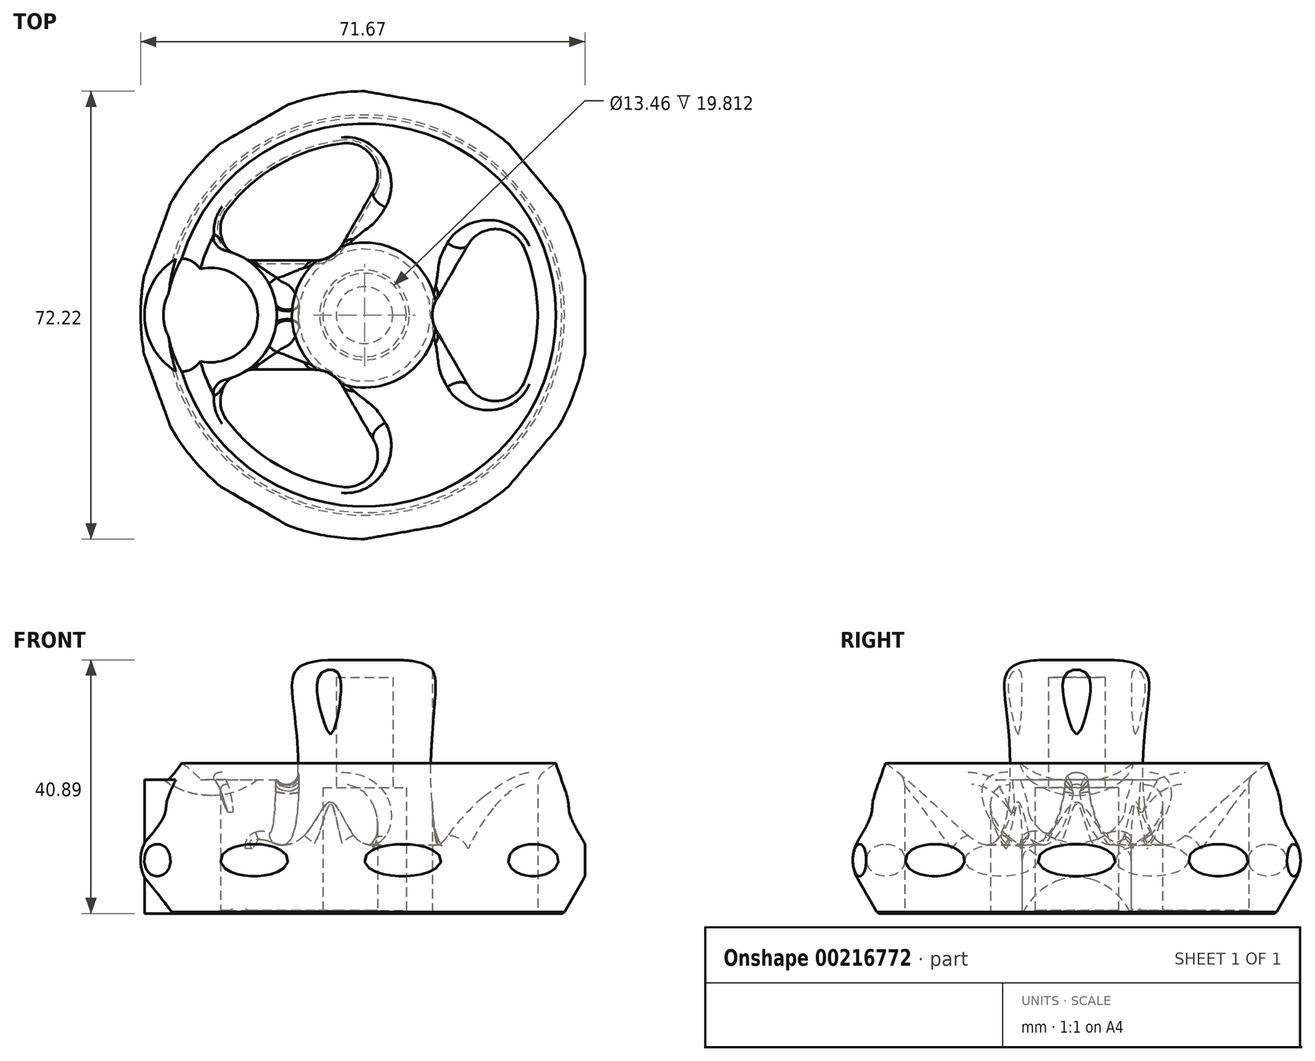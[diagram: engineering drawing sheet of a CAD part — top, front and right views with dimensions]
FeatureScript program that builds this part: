
annotation { "Feature Type Name" : "Feature", "Feature Type Description" : "" }
export const myFeature = defineFeature(function(context is Context, id is Id, definition is map)
    precondition{}
    {
        {
            var Q0;
            Q0=qCreatedBy(makeId("Front.planeOp"),FACE);
            var sketch = newSketch(context, id + "F0", { "sketchPlane" : qUnion([Q0])});
            skLineSegment(sketch, "E0", {"start": v(6.73, 0) * mm, "end": v(32.13, 0) * mm});
            skLineSegment(sketch, "E1", {"start": v(0, 40.64) * mm, "end": v(0, 38.1) * mm});
            skLineSegment(sketch, "E2", {"start": v(0, 38.1) * mm, "end": v(4.57, 38.1) * mm});
            skLineSegment(sketch, "E3", {"start": v(6.73, 20.32) * mm, "end": v(6.73, 0) * mm});
            skFitSpline(sketch, "E4", {"points": [v(35.65, 24.88) * mm, v(14.9, 11.07) * mm, v(10.97, 29.16) * mm, v(10.85, 39.41) * mm, v(0, 40.64) * mm], "startDerivative": vector(-45.35, 35.18) * mm, "endDerivative": vector(-73, -6.21) * mm});
            skPoint(sketch, "E5.orphan", {"position": v(0, 77.97) * mm});
            skLineSegment(sketch, "E6", {"start": v(0, -42.76) * mm, "end": v(0, 58.59) * mm, "construction": true});
            skLineSegment(sketch, "E7", {"start": v(4.57, 38.1) * mm, "end": v(4.57, 20.32) * mm});
            skLineSegment(sketch, "E8", {"start": v(4.57, 20.32) * mm, "end": v(6.73, 20.32) * mm});
            skPoint(sketch, "E9.orphan", {"position": v(11.05, 17.05) * mm});
            skLineSegment(sketch, "E10", {"start": v(32.13, 0) * mm, "end": v(35.26, 5.42) * mm});
            skPoint(sketch, "E11.visualSharp", {"position": v(28.42, 22.4) * mm});
            skPoint(sketch, "E12.visualSharp", {"position": v(35.56, 5.94) * mm});
            skLineSegment(sketch, "E13", {"start": v(37.21, 8.8) * mm, "end": v(30.06, 35.48) * mm, "construction": true});
            skFitSpline(sketch, "E14", {"points": [v(37.21, 8.8) * mm, v(32.84, 18.2) * mm, v(30.88, 24.23) * mm], "startDerivative": vector(-26.8, 39.37) * mm, "endDerivative": vector(-3.75, 13.08) * mm});
            skArc(sketch, "E15.filletArc", {"start": v(33.08, 16.25) * mm, "mid": v(29.56, 20.04) * mm, "end": v(24.55, 18.79) * mm});
            skArc(sketch, "E16.filletArc", {"start": v(35.26, 5.42) * mm, "mid": v(36.11, 8.69) * mm, "end": v(35.16, 11.93) * mm});
            skSolve(sketch);
        }
        {
            var Q0;
            Q0=qSketchRegion(id+"F0",true);
            var Q1;
            Q1=sQuery(id+"F0.wireOp",EDGE,"E6");
            revolve(context, id + "F1", {"entities" : qUnion([Q0]), "axis" : qUnion([Q1]), "revolveType" : RevolveType.SYMMETRIC, "angle" : 120 * degree});
        }
        {
            var Q0;
            Q0=qCreatedBy(makeId("Top.planeOp"),FACE);
            var sketch = newSketch(context, id + "F2", { "sketchPlane" : qUnion([Q0])});
            skArc(sketch, "E17", {"start": v(25.8, -10.75) * mm, "mid": v(27.94, 0) * mm, "end": v(25.8, 10.75) * mm});
            skLineSegment(sketch, "E18", {"start": v(11.63, 2.54) * mm, "end": v(16.7, 11.33) * mm});
            skLineSegment(sketch, "E19", {"start": v(11.63, -2.54) * mm, "end": v(16.7, -11.33) * mm});
            skPoint(sketch, "E20.visualSharp", {"position": v(20.88, 18.57) * mm});
            skArc(sketch, "E20.filletArc", {"start": v(25.8, 10.75) * mm, "mid": v(21.43, 13.86) * mm, "end": v(16.7, 11.33) * mm});
            skPoint(sketch, "E21.visualSharp", {"position": v(20.88, -18.57) * mm});
            skArc(sketch, "E21.filletArc", {"start": v(16.7, -11.33) * mm, "mid": v(21.43, -13.86) * mm, "end": v(25.8, -10.75) * mm});
            skPoint(sketch, "E22.visualSharp", {"position": v(10.16, 0) * mm});
            skArc(sketch, "E22.filletArc", {"start": v(11.63, 2.54) * mm, "mid": v(10.95, 0) * mm, "end": v(11.63, -2.54) * mm});
            skSolve(sketch);
        }
        {
            var Q0;
            Q0=qSketchRegion(id+"F2",true);
            extrude(context, id + "F3", {"entities" : qUnion([Q0]), "operationType" : NewBodyOperationType.REMOVE, "endBound" : BoundingType.THROUGH_ALL, "depth" : 25.4 * mm});
        }
        {
            var Q0;
            Q0=makeQuery(id+"F3.boolean.opBoolean","INTERSECT",EDGE,{"derivedFrom":[makeQuery(id+"F1.opRevolve","SWEPT_FACE",FACE,{"disambiguationData":[OSD([sQuery(id+"F0.wireOp",EDGE,"E4")])]}),makeQuery(id+"F3.opExtrude","SWEPT_FACE",FACE,{"disambiguationData":[OSD([sQuery(id+"F2.wireOp",EDGE,"E17")])]})]});
            fillet(context, id + "F4", {"entities" : qUnion([Q0]), "radius" : 2.54 * mm, "tangentPropagation" : true, "allowEdgeOverflow" : false});
        }
        {
            var Q0;
            Q0=qCreatedBy(makeId("Top.planeOp"),FACE);
            var sketch = newSketch(context, id + "F5", { "sketchPlane" : qUnion([Q0])});
            skLineSegment(sketch, "E23", {"start": v(35.56, -10.16) * mm, "end": v(35.56, 10.16) * mm});
            skLineSegment(sketch, "E24", {"start": v(35.56, 10.16) * mm, "end": v(39.7, 10.16) * mm});
            skLineSegment(sketch, "E25", {"start": v(39.7, 10.16) * mm, "end": v(39.7, -10.16) * mm});
            skLineSegment(sketch, "E26", {"start": v(39.7, -10.16) * mm, "end": v(35.56, -10.16) * mm});
            skSolve(sketch);
        }
        {
            var Q0;
            Q0=qSketchRegion(id+"F5",true);
            extrude(context, id + "F6", {"entities" : qUnion([Q0]), "depth" : 25.4 * mm});
        }
        {
            var Q0;
            Q0=makeQuery(id+"F6.opExtrude","SWEPT_BODY",BODY,{"disambiguationData":[OSD([sQuery(id+"F5.wireOp",EDGE,"E23"),sQuery(id+"F5.wireOp",EDGE,"E24"),sQuery(id+"F5.wireOp",EDGE,"E25"),sQuery(id+"F5.wireOp",EDGE,"E26")])]});
            var Q1;
            Q1=sQuery(id+"F0.wireOp",EDGE,"E6");
            circularPattern(context, id + "F7", {"operationType" : NewBodyOperationType.REMOVE, "entities" : qUnion([Q0]), "axis" : qUnion([Q1]), "angle" : 360 * degree, "instanceCount" : 9, "equalSpace" : true});
        }
        {
            var Q0;
            Q0=makeQuery(id+"F1.opRevolve","SWEPT_BODY",BODY,{"disambiguationData":[OSD([sQuery(id+"F0.wireOp",EDGE,"E0"),sQuery(id+"F0.wireOp",EDGE,"dpCK8SRb-WdQn-L2Cs-7aav-e22ffPn0EV3C"),sQuery(id+"F0.wireOp",EDGE,"99iCUp3l-W3Re-Ts3m-6MKF-OaPGGpgDnCRw"),sQuery(id+"F0.wireOp",EDGE,"E1"),sQuery(id+"F0.wireOp",EDGE,"E2"),sQuery(id+"F0.wireOp",EDGE,"E3"),sQuery(id+"F0.wireOp",EDGE,"E4")])]});
            var Q1;
            Q1=sQuery(id+"F0.wireOp",EDGE,"E6");
            circularPattern(context, id + "F8", {"operationType" : NewBodyOperationType.ADD, "entities" : qUnion([Q0]), "axis" : qUnion([Q1]), "angle" : 360 * degree, "instanceCount" : 3, "equalSpace" : true});
        }
        {
            var Q0;
            Q0=makeQuery(id+"F8.opPattern","COPY",FACE,{"derivedFrom":makeQuery(id+"F3.boolean.opBoolean","COPY",FACE,{"derivedFrom":makeQuery(id+"F3.opExtrude","SWEPT_FACE",FACE,{"disambiguationData":[OSD([sQuery(id+"F2.wireOp",EDGE,"E18")])]})}),"instanceName":"1"});
            var Q1;
            {var subQ0=makeQuery(id+"F1.opRevolve","SWEPT_EDGE",EDGE,{"disambiguationData":[OSD([sQuery(id+"F0.wireOp",EDGE,"E0"),sQuery(id+"F0.wireOp",EDGE,"E3")])]});Q1=makeQuery(id+"F8.boolean.opBoolean","MERGE",EDGE,{"derivedFrom":[subQ0,makeQuery(id+"F8.opPattern","COPY",EDGE,{"derivedFrom":subQ0,"instanceName":"1"}),makeQuery(id+"F8.opPattern","COPY",EDGE,{"derivedFrom":subQ0,"instanceName":"2"})]});}
            var Q2;
            Q2=makeQuery(id+"F3.boolean.opBoolean","COPY",EDGE,{"derivedFrom":makeQuery(id+"F3.opExtrude","CAP_EDGE",EDGE,{"disambiguationData":[OSD([sQuery(id+"F2.wireOp",EDGE,"E18")])],"isStart":true})});
            var Q3;
            Q3=makeQuery(id+"F8.opPattern","COPY",EDGE,{"derivedFrom":makeQuery(id+"F3.boolean.opBoolean","COPY",EDGE,{"derivedFrom":makeQuery(id+"F3.opExtrude","CAP_EDGE",EDGE,{"disambiguationData":[OSD([sQuery(id+"F2.wireOp",EDGE,"E19")])],"isStart":true})}),"instanceName":"2"});
            var Q4;
            {var subQ0=makeQuery(id+"F1.opRevolve","SWEPT_EDGE",EDGE,{"disambiguationData":[OSD([sQuery(id+"F0.wireOp",EDGE,"E0"),sQuery(id+"F0.wireOp",EDGE,"vpSZ5KzX-oGi7-IppH-yeRc-xyXKcn8NRoAp")])]});Q4=makeQuery(id+"F8.boolean.opBoolean","MERGE",EDGE,{"derivedFrom":[subQ0,makeQuery(id+"F8.opPattern","COPY",EDGE,{"derivedFrom":subQ0,"instanceName":"1"}),makeQuery(id+"F8.opPattern","COPY",EDGE,{"derivedFrom":subQ0,"instanceName":"2"})]});}
            chamfer(context, id + "F9", {"entities" : qUnion([Q0, Q1, Q2, Q3, Q4]), "width" : 0.5 * mm, "tangentPropagation" : true});
        }
        {
            var Q0;
            Q0=qCreatedBy(makeId("Top.planeOp"),FACE);
            var sketch = newSketch(context, id + "F10", { "sketchPlane" : qUnion([Q0])});
            skCircle(sketch, "E27", {"center": v(-24.82, 0) * mm, "radius": 10.67 * mm});
            skSolve(sketch);
        }
        {
            var Q0;
            Q0=qSketchRegion(id+"F10",true);
            extrude(context, id + "F11", {"entities" : qUnion([Q0]), "operationType" : NewBodyOperationType.ADD, "depth" : 21.59 * mm});
        }
        {
            var Q0;
            Q0=qCreatedBy(makeId("Front.planeOp"),FACE);
            var sketch = newSketch(context, id + "F12", { "sketchPlane" : qUnion([Q0])});
            skLineSegment(sketch, "E28", {"start": v(-24.82, 21.59) * mm, "end": v(-24.82, 38.4) * mm, "construction": true});
            skLineSegment(sketch, "E29", {"start": v(-24.82, 31.75) * mm, "end": v(-24.82, 19.05) * mm});
            skArc(sketch, "E30", {"start": v(-37.52, 31.75) * mm, "mid": v(-33.8, 22.77) * mm, "end": v(-24.82, 19.05) * mm});
            skPoint(sketch, "E31.orphan", {"position": v(-32.35, 21.59) * mm});
            skLineSegment(sketch, "E32", {"start": v(-24.82, 19.05) * mm, "end": v(-24.82, 31.75) * mm});
            skLineSegment(sketch, "E33", {"start": v(-37.52, 31.75) * mm, "end": v(-24.82, 31.75) * mm});
            skSolve(sketch);
        }
        {
            var Q0;
            Q0=qSketchRegion(id+"F12",true);
            var Q1;
            Q1=sQuery(id+"F12.wireOp",EDGE,"E28");
            revolve(context, id + "F13", {"operationType" : NewBodyOperationType.REMOVE, "entities" : qUnion([Q0]), "axis" : qUnion([Q1]), "revolveType" : RevolveType.FULL, "oppositeDirection" : true});
        }
        {
            var Q0;
            {var subQ0=makeQuery(id+"F1.opRevolve","SWEPT_FACE",FACE,{"disambiguationData":[OSD([sQuery(id+"F0.wireOp",EDGE,"E4")])]});Q0=makeQuery(id+"F11.boolean.opBoolean","INTERSECT",EDGE,{"derivedFrom":[makeQuery(id+"F8.boolean.opBoolean","MERGE",FACE,{"derivedFrom":[subQ0,makeQuery(id+"F8.opPattern","COPY",FACE,{"derivedFrom":subQ0,"instanceName":"1"}),makeQuery(id+"F8.opPattern","COPY",FACE,{"derivedFrom":subQ0,"instanceName":"2"})]}),makeQuery(id+"F11.opExtrude","SWEPT_FACE",FACE,{"disambiguationData":[OSD([sQuery(id+"F10.wireOp",EDGE,"E27")])]})]});}
            var Q1;
            {var subQ0=makeQuery(id+"F1.opRevolve","SWEPT_FACE",FACE,{"disambiguationData":[OSD([sQuery(id+"F0.wireOp",EDGE,"E15.filletArc")])]});Q1=makeQuery(id+"F11.boolean.opBoolean","INTERSECT",EDGE,{"disambiguationData":[OD(1.0)],"derivedFrom":[makeQuery(id+"F8.boolean.opBoolean","MERGE",FACE,{"derivedFrom":[subQ0,makeQuery(id+"F8.opPattern","COPY",FACE,{"derivedFrom":subQ0,"instanceName":"1"}),makeQuery(id+"F8.opPattern","COPY",FACE,{"derivedFrom":subQ0,"instanceName":"2"})]}),makeQuery(id+"F11.opExtrude","SWEPT_FACE",FACE,{"disambiguationData":[OSD([sQuery(id+"F10.wireOp",EDGE,"E27")])]})]});}
            fillet(context, id + "F14", {"entities" : qUnion([Q0, Q1]), "radius" : 1.9 * mm, "tangentPropagation" : true, "allowEdgeOverflow" : false});
        }
    });
